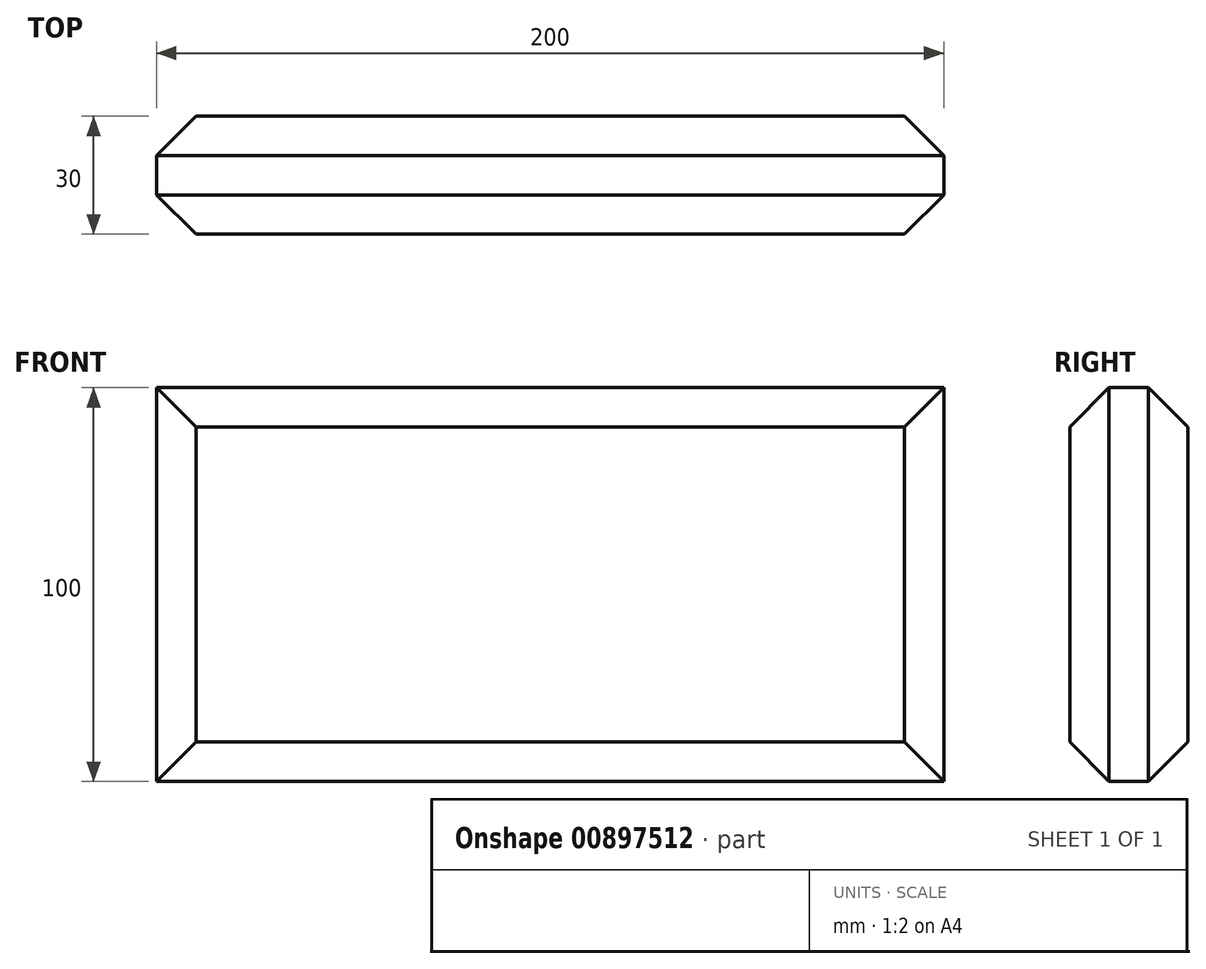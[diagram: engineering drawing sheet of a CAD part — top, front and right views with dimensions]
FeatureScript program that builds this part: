
annotation { "Feature Type Name" : "Feature", "Feature Type Description" : "" }
export const myFeature = defineFeature(function(context is Context, id is Id, definition is map)
    precondition{}
    {
        {
            var Q0;
            Q0=qCreatedBy(makeId("Front.planeOp"),FACE);
            var sketch = newSketch(context, id + "F0", { "sketchPlane" : qUnion([Q0])});
            skLineSegment(sketch, "E0.bottom", {"start": v(-100, -50) * mm, "end": v(100, -50) * mm});
            skLineSegment(sketch, "E0.top", {"start": v(-100, 50) * mm, "end": v(100, 50) * mm});
            skLineSegment(sketch, "E0.left", {"start": v(-100, -50) * mm, "end": v(-100, 50) * mm});
            skLineSegment(sketch, "E0.right", {"start": v(100, -50) * mm, "end": v(100, 50) * mm});
            skPoint(sketch, "E0.middle", {"position": v(0, 0) * mm});
            skSolve(sketch);
        }
        {
            var Q0;
            Q0=makeQuery(id+"F0.imprint","IMPRINT",FACE,{"disambiguationData":[TD([[makeQuery(id+"F0.imprint","IMPRINT",EDGE,{"derivedFrom":sQuery(id+"F0.wireOp",EDGE,"E0.bottom")}),1.0]])]});
            extrude(context, id + "F1", {"entities" : qUnion([Q0]), "depth" : 30 * mm, "offsetDistance" : 25.4 * mm});
        }
        {
            var Q0;
            Q0=makeQuery(id+"F1.opExtrude","CAP_EDGE",EDGE,{"disambiguationData":[OSD([sQuery(id+"F0.wireOp",EDGE,"E0.top")])],"isStart":false});
            var Q1;
            Q1=makeQuery(id+"F1.opExtrude","CAP_EDGE",EDGE,{"disambiguationData":[OSD([sQuery(id+"F0.wireOp",EDGE,"E0.bottom")])],"isStart":false});
            var Q2;
            Q2=makeQuery(id+"F1.opExtrude","CAP_EDGE",EDGE,{"disambiguationData":[OSD([sQuery(id+"F0.wireOp",EDGE,"E0.right")])],"isStart":false});
            var Q3;
            Q3=makeQuery(id+"F1.opExtrude","CAP_EDGE",EDGE,{"disambiguationData":[OSD([sQuery(id+"F0.wireOp",EDGE,"E0.left")])],"isStart":false});
            var Q4;
            Q4=makeQuery(id+"F1.opExtrude","CAP_EDGE",EDGE,{"disambiguationData":[OSD([sQuery(id+"F0.wireOp",EDGE,"E0.left")])],"isStart":true});
            var Q5;
            Q5=makeQuery(id+"F1.opExtrude","CAP_EDGE",EDGE,{"disambiguationData":[OSD([sQuery(id+"F0.wireOp",EDGE,"E0.top")])],"isStart":true});
            var Q6;
            Q6=makeQuery(id+"F1.opExtrude","CAP_EDGE",EDGE,{"disambiguationData":[OSD([sQuery(id+"F0.wireOp",EDGE,"E0.bottom")])],"isStart":true});
            var Q7;
            Q7=makeQuery(id+"F1.opExtrude","CAP_EDGE",EDGE,{"disambiguationData":[OSD([sQuery(id+"F0.wireOp",EDGE,"E0.right")])],"isStart":true});
            chamfer(context, id + "F2", {"entities" : qUnion([Q0, Q1, Q2, Q3, Q4, Q5, Q6, Q7]), "chamferType" : ChamferType.OFFSET_ANGLE, "width" : 10 * mm, "oppositeDirection" : false, "angle" : 45 * degree, "tangentPropagation" : true});
        }
    });
